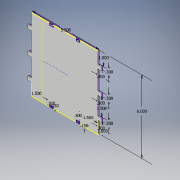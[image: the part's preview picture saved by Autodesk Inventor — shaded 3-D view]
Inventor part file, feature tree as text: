
AUTODESK INVENTOR PART (.ipt)
format: ipt  version: 2018 (Build 220112000, 112)  size: 162,304 bytes
history: native  units: in
note: dims shown in document units (in); Inventor stores cm internally (conversion verified against a paired STEP export)
features: sketch x2, extrude x2
ambient origin geometry x8: Origin, YZ Plane, XZ Plane, XY Plane, X Axis, Y Axis, Z Axis, Center Point
bodies: Solid1 (feature_tree)
feature tree (4):
  sketch  "Sketch1"  dims[d0=5.5in d1=6.0in]
  extrude  "Extrusion1"  Depth=6.0in
  extrude  "Extrusion3"  Depth=0.3in
  sketch  "Sketch2"  dims[d2=0.3in d3=0.3in d4=1.0in d5=0.3in d6=0.3in d7=0.3in d8=0.3in d9=1.0in d10=1.5in d11=0.1in d12=0.0in d13=0.15in d14=0.3in d15=1.5in d16=0.3in d17=0.15in d18=1.5in d21=1.0in d22=0.0in]
